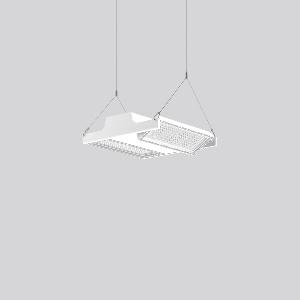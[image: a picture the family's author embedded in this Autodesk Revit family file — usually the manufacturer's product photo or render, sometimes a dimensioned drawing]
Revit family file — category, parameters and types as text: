
# Revit family: light_case_921682_002_1_76_a710
name_source: partatom
category: Lighting Fixtures
units: mm (PartAtom-declared; Revit-internal decimal feet)

## family parameters
Cut with Voids When Loaded = No
Host = Face
Light Source = No
Part Type = Normal
Room Calculation Point = No
Round Connector Dimension = Use Diameter
Shared = No

## types (1)
- LIGHT CASE (1 x LED Modul 865, 8700 lm, 6500)
    Apparent Load = 117 VA
    CIE Flux Codes = 80 98 100 100 100
    Color Rendering = 80
    Color Temperature = 6500
    Default Elevation = 1800 mm
    Description = Series: LIGHT CASE
Flat highbay luminaire for chain or cable suspension with 2 LED modules that can be swivelled. Housing: die cast aluminium and sheet steel, powder-coated. Optimised thermal management thanks to special luminaire design. Self-cleaning heat sink for constant heat dissipation. Cover: plastic (polycarbonate, shockproof), with integrated four-row lens system. LED modules can be swivelled ± 30° for optimum illumination. Suitable for chain or steel cable suspension (to be provided on site). With 5-pin connection terminal (1.5 m). With integrated movement sensor and light sensor for daylight detection on request. Ball impact proof in accordance with DIN 18032-03 (except steel cable suspension). Luminaire with limited surface temperature in accordance with EN 60598-2-24 for use in environments in which a deposit of conductive dust on the luminaire can be expected. 
Colour: white
Length: 406 mm
Width: 397 mm
Height: 110 mm
Lamp: LED
Socket: without socket
Colour temperature: 6500K
Colour rendering index (CRI): 80
System power: 117 W
Rated luminous flux: 17400 lm
Luminous efficiency: 149 lm/W
Control gear: Converter, dimmable, DALI
Protection class: I
Type of protection: IP 65
    Height = 110 mm
    Lamp = 1 x LED Modul 865
    Lamp Light Flux = 8700 lm
    Lamp count = 1
    Length = 406 mm
    Lifetime = 50000 h
    Luminous efficacy = 149 lm/W
    Manufacturer = RZB
    ModVariant = No
    Model = 921682.002.1.76
    Mounting Place = Ceiling
    Mounting Type = Pendant
    Number of Poles = 1
    OnlyDefault = Yes
    Power Factor = 1
    Product Name = LIGHT CASE
    Product group = Pendant commercial luminaires
    ProductGroupID = 903
    Protection Class = Protection class I
    Protection Degree = IP 65
    RLX_Detail_Level = 1
    RLX_Emergency_Light_Flux = 0 lm
    RLX_Emergency_Type = 0
    RLX_Emergency_Type_DB = No
    RlxData = <blob elided: 24181 chars, md5=30087c51>
    Socket = socket
    Standby Power = 0 W
    System Light Flux = 17400 lm
    System Power = 117 W
    Type Comments = Product without accessories
    Type Image = 921517.002.76.jpg
    URL = http://relux.com
    VarID = ---
    Voltage = 230 V
    Voltage Range = 220-240 V
    Weight = 0.00 kg
    Width = 397 mm

## geometry (parser evidence)
native form markers: Blend x4, Sweep x17
no freeform markers — native parametric forms only
